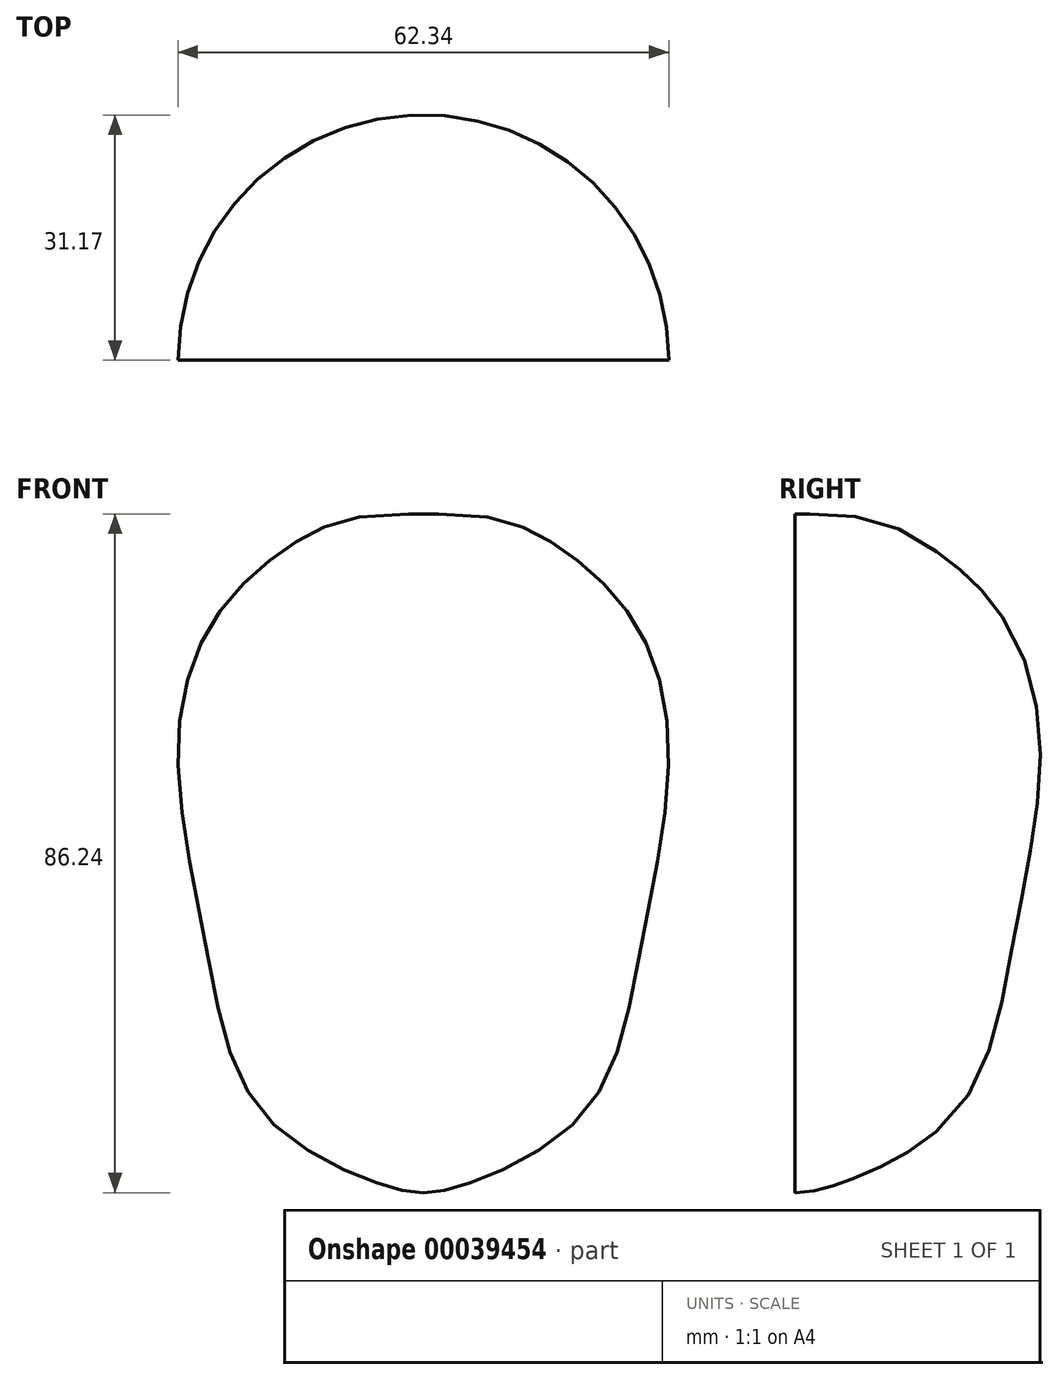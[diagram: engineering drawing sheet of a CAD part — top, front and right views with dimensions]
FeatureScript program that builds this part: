
annotation { "Feature Type Name" : "Feature", "Feature Type Description" : "" }
export const myFeature = defineFeature(function(context is Context, id is Id, definition is map)
    precondition{}
    {
        {
            var Q0;
            Q0=qCreatedBy(makeId("Front.planeOp"),FACE);
            var sketch = newSketch(context, id + "F0", { "sketchPlane" : qUnion([Q0])});
            skFitSpline(sketch, "E0", {"points": [v(0, 66.33) * mm, v(-16.65, 62.5) * mm, v(-26.14, 53.61) * mm, v(-31.15, 37.27) * mm, v(-27.7, 11.7) * mm, v(-20.6, -9.48) * mm, v(-6.13, -18.56) * mm, v(0, -19.88) * mm], "startDerivative": vector(-188.8, 5.37) * mm, "endDerivative": vector(60.34, 0.1) * mm});
            skFitSpline(sketch, "E1.MirrorCS", {"points": [v(0, 66.33) * mm, v(16.65, 62.5) * mm, v(26.14, 53.61) * mm, v(31.15, 37.27) * mm, v(27.7, 11.7) * mm, v(20.6, -9.48) * mm, v(6.13, -18.56) * mm, v(0, -19.88) * mm], "startDerivative": vector(188.8, 5.37) * mm, "endDerivative": vector(-60.34, 0.1) * mm});
            skSolve(sketch);
        }
        {
            var Q0;
            Q0=qCreatedBy(makeId("Front.planeOp"),FACE);
            var sketch = newSketch(context, id + "F1", { "sketchPlane" : qUnion([Q0])});
            skLineSegment(sketch, "E2", {"start": v(0, 92.61) * mm, "end": v(0, -63.56) * mm});
            skSolve(sketch);
        }
        {
            var Q0;
            Q0=makeQuery(id+"F0.imprint","IMPRINT",FACE,{"disambiguationData":[TD([[makeQuery(id+"F0.imprint","IMPRINT",EDGE,{"derivedFrom":sQuery(id+"F0.wireOp",EDGE,"E0")}),1.0]])]});
            var Q1;
            Q1=sQuery(id+"F0.wireOp",EDGE,"E0");
            var Q2;
            Q2=sQuery(id+"F1.wireOp",EDGE,"E2");
            revolve(context, id + "F2", {"bodyType" : ToolBodyType.SURFACE, "entities" : qUnion([Q0]), "surfaceEntities" : qUnion([Q1]), "axis" : qUnion([Q2]), "revolveType" : RevolveType.ONE_DIRECTION, "angle" : 180 * degree});
        }
    });
